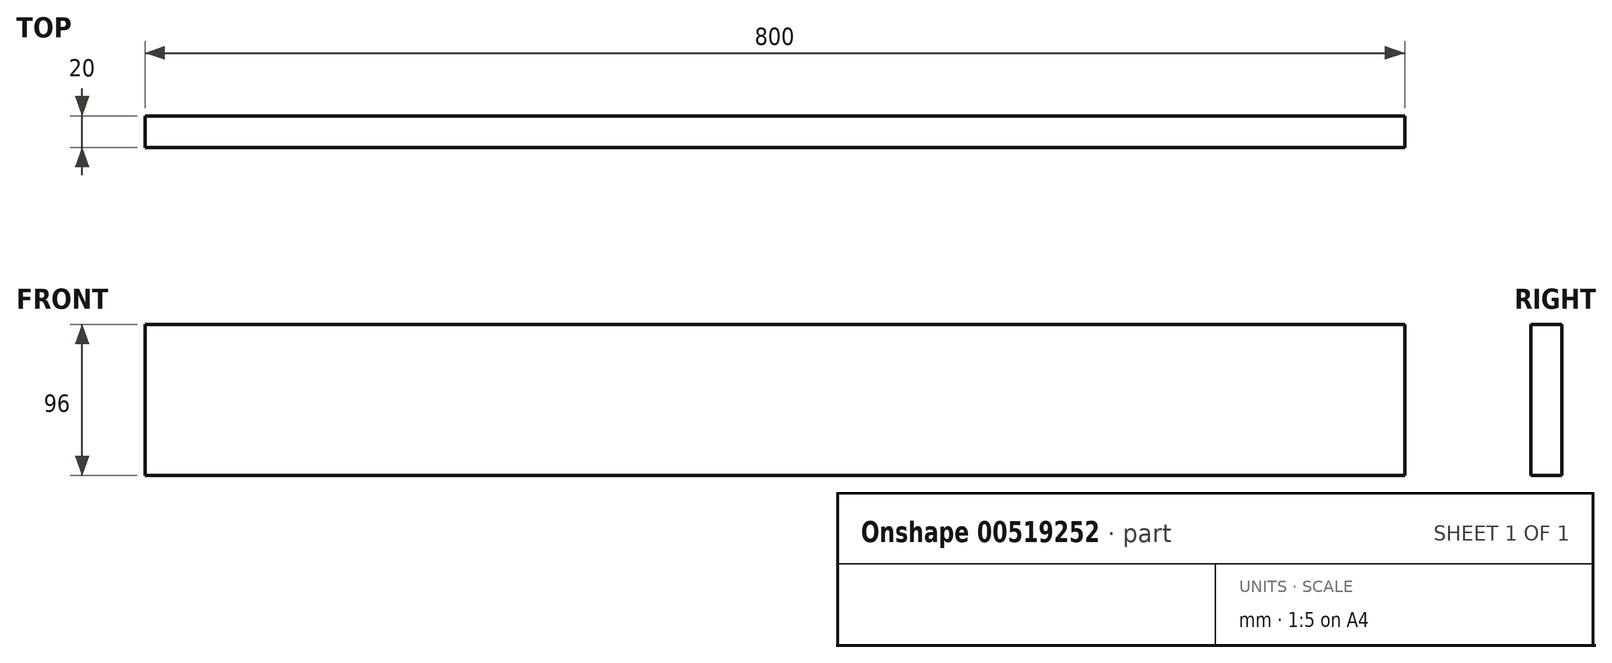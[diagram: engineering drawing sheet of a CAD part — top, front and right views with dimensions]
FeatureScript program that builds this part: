
annotation { "Feature Type Name" : "Feature", "Feature Type Description" : "" }
export const myFeature = defineFeature(function(context is Context, id is Id, definition is map)
    precondition{}
    {
        {
            var Q0;
            Q0=qCreatedBy(makeId("Right.planeOp"),FACE);
            var sketch = newSketch(context, id + "F0", { "sketchPlane" : qUnion([Q0])});
            skLineSegment(sketch, "E0.bottom", {"start": v(0, 0) * mm, "end": v(20, 0) * mm});
            skLineSegment(sketch, "E0.top", {"start": v(0, 96) * mm, "end": v(20, 96) * mm});
            skLineSegment(sketch, "E0.left", {"start": v(0, 0) * mm, "end": v(0, 96) * mm});
            skLineSegment(sketch, "E0.right", {"start": v(20, 0) * mm, "end": v(20, 96) * mm});
            skSolve(sketch);
        }
        {
            var Q0;
            Q0=qSketchRegion(id+"F0",true);
            extrude(context, id + "F1", {"entities" : qUnion([Q0]), "oppositeDirection" : true, "depth" : 800 * mm, "offsetDistance" : 25 * mm});
        }
    });
